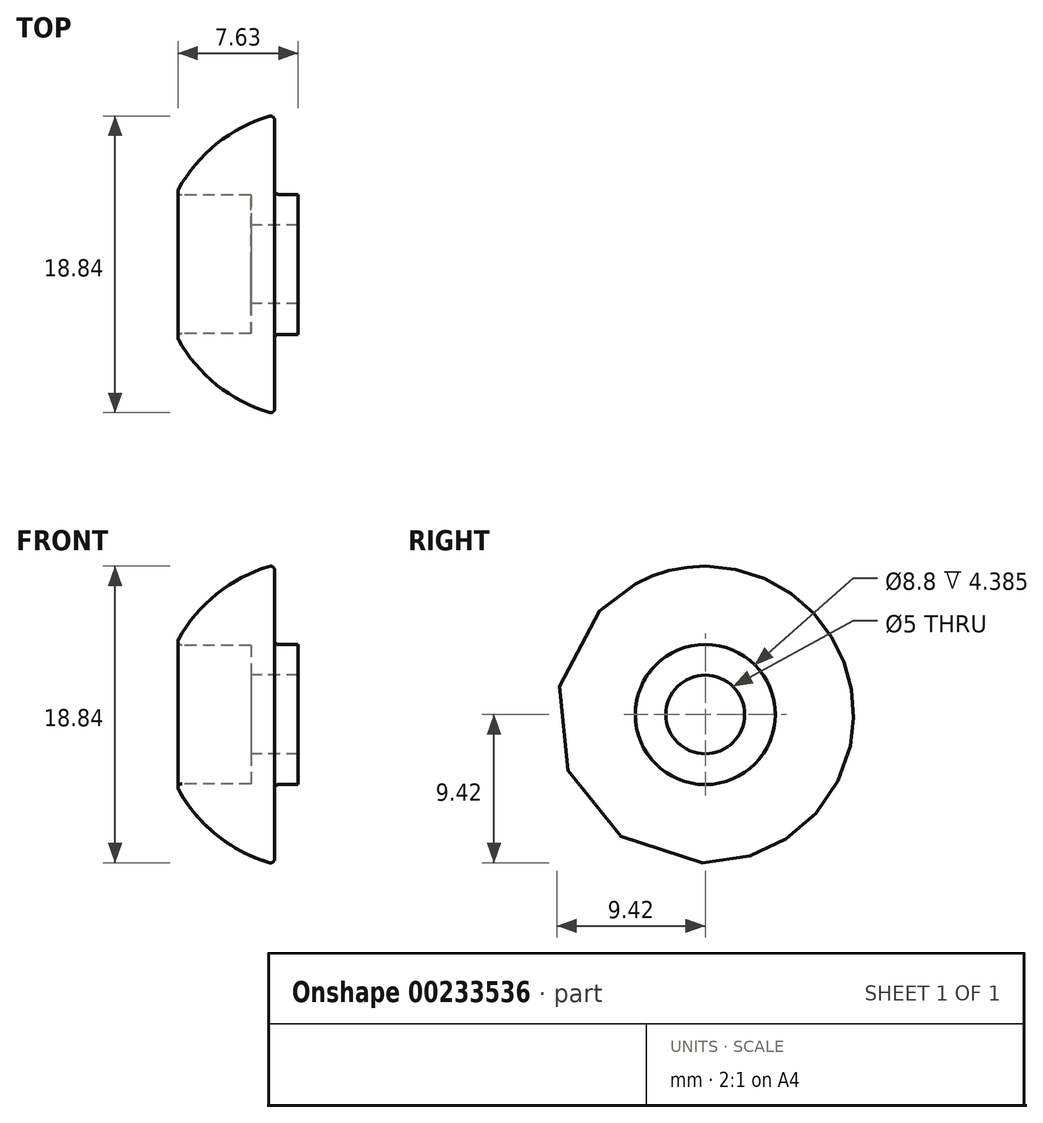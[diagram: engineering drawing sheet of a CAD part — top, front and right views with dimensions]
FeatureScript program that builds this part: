
annotation { "Feature Type Name" : "Feature", "Feature Type Description" : "" }
export const myFeature = defineFeature(function(context is Context, id is Id, definition is map)
    precondition{}
    {
        {
            var Q0;
            Q0=qCreatedBy(makeId("Top.planeOp"),FACE);
            var sketch = newSketch(context, id + "F0", { "sketchPlane" : qUnion([Q0])});
            skLineSegment(sketch, "E0", {"start": v(-82.6, 0) * mm, "end": v(124.14, 0) * mm, "construction": true});
            skLineSegment(sketch, "E1", {"start": v(124.14, 2.5) * mm, "end": v(8.84, 2.5) * mm, "construction": true});
            skLineSegment(sketch, "E2", {"start": v(7.34, 4.45) * mm, "end": v(7.34, 9.5) * mm});
            skLineSegment(sketch, "E3", {"start": v(7.34, 9.5) * mm, "end": v(18.24, 12.34) * mm, "construction": true});
            skLineSegment(sketch, "E4", {"start": v(0, 0) * mm, "end": v(0, -9.73) * mm, "construction": true});
            skArc(sketch, "E5", {"start": v(1.04, 4.4) * mm, "mid": v(3.64, 7.63) * mm, "end": v(7.34, 9.5) * mm});
            skLineSegment(sketch, "E6", {"start": v(7.34, 4.45) * mm, "end": v(8.84, 4.45) * mm});
            skLineSegment(sketch, "E7", {"start": v(8.84, 4.45) * mm, "end": v(8.84, 2.5) * mm});
            skPoint(sketch, "E8.orphan", {"position": v(7.34, 2.5) * mm});
            skLineSegment(sketch, "E9", {"start": v(0, 0) * mm, "end": v(124.14, 0) * mm});
            skLineSegment(sketch, "E10", {"start": v(1.04, 4.4) * mm, "end": v(1.04, 0) * mm, "construction": true});
            skLineSegment(sketch, "E11", {"start": v(5.84, 2.5) * mm, "end": v(8.84, 2.5) * mm});
            skLineSegment(sketch, "E12", {"start": v(1.04, 4.4) * mm, "end": v(5.84, 4.4) * mm});
            skLineSegment(sketch, "E13", {"start": v(5.84, 4.4) * mm, "end": v(5.84, 2.5) * mm});
            skSolve(sketch);
        }
        {
            var Q0;
            Q0=qSketchRegion(id+"F0",true);
            var Q1;
            Q1=sQuery(id+"F0.wireOp",EDGE,"E0");
            revolve(context, id + "F1", {"entities" : qUnion([Q0]), "axis" : qUnion([Q1]), "revolveType" : RevolveType.FULL});
        }
        {
            var Q0;
            Q0=makeQuery(id+"F1.opRevolve","SWEPT_EDGE",EDGE,{"disambiguationData":[OSD([sQuery(id+"F0.wireOp",EDGE,"E2"),sQuery(id+"F0.wireOp",EDGE,"E5")])]});
            var Q1;
            Q1=makeQuery(id+"F1.opRevolve","SWEPT_EDGE",EDGE,{"disambiguationData":[OSD([sQuery(id+"F0.wireOp",EDGE,"E2"),sQuery(id+"F0.wireOp",EDGE,"E6")])]});
            var Q2;
            Q2=makeQuery(id+"F1.opRevolve","SWEPT_EDGE",EDGE,{"disambiguationData":[OSD([sQuery(id+"F0.wireOp",EDGE,"E5"),sQuery(id+"F0.wireOp",EDGE,"E12")])]});
            fillet(context, id + "F2", {"entities" : qUnion([Q0, Q1, Q2]), "radius" : 0.25 * mm, "tangentPropagation" : true, "allowEdgeOverflow" : false});
        }
    });
